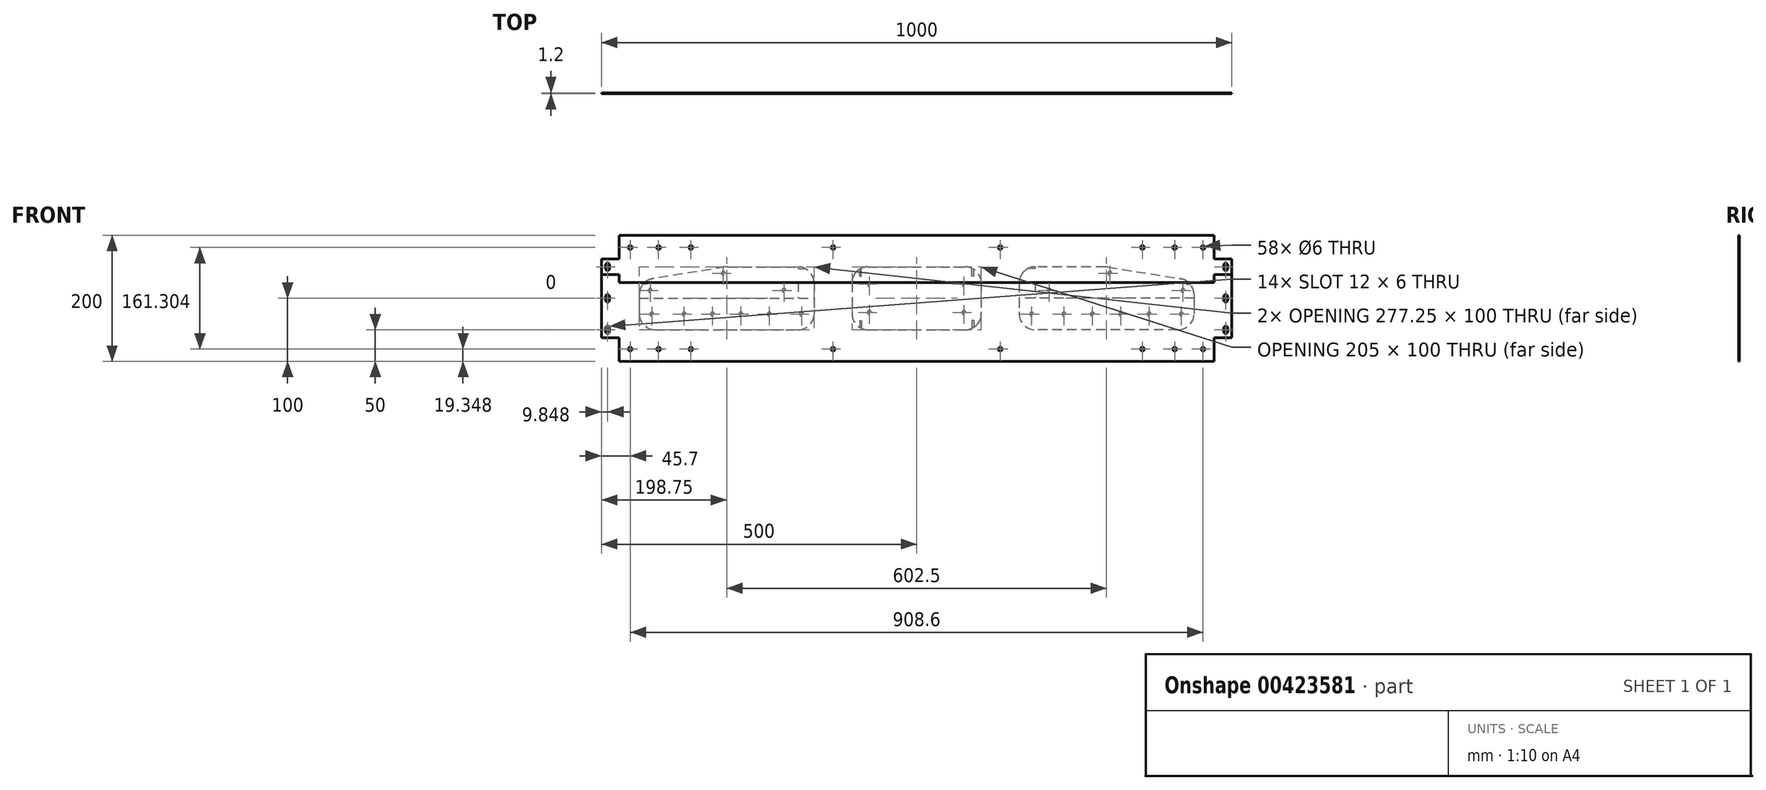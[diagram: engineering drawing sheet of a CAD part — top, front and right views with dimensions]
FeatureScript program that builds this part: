
annotation { "Feature Type Name" : "Feature", "Feature Type Description" : "" }
export const myFeature = defineFeature(function(context is Context, id is Id, definition is map)
    precondition{}
    {
        {
            assignVariable(context, id + "F0", {"name" : "eTole", "anyValue" : 0.8});
        }
        {
            var Q0;
            Q0=qCreatedBy(makeId("Front.planeOp"),FACE);
            var sketch = newSketch(context, id + "F1", { "sketchPlane" : qUnion([Q0])});
            skLineSegment(sketch, "E0.bottom", {"start": v(-471.9, 100) * mm, "end": v(471.9, 100) * mm});
            skLineSegment(sketch, "E0.top", {"start": v(-471.9, -100) * mm, "end": v(471.9, -100) * mm});
            skLineSegment(sketch, "E0.left", {"start": v(-500, 62.4) * mm, "end": v(-500, -62.4) * mm});
            skLineSegment(sketch, "E0.right", {"start": v(500, 62.4) * mm, "end": v(500, -62.4) * mm});
            skLineSegment(sketch, "E1.bottom", {"start": v(-471.9, 62.4) * mm, "end": v(471.9, 62.4) * mm, "construction": true});
            skLineSegment(sketch, "E1.top", {"start": v(-471.9, -62.4) * mm, "end": v(471.9, -62.4) * mm, "construction": true});
            skLineSegment(sketch, "E1.left", {"start": v(-471.9, 62.4) * mm, "end": v(-471.9, -62.4) * mm, "construction": true});
            skLineSegment(sketch, "E1.right", {"start": v(471.9, 62.4) * mm, "end": v(471.9, -62.4) * mm, "construction": true});
            skLineSegment(sketch, "E2.bottom", {"start": v(-77, 50) * mm, "end": v(77, 50) * mm});
            skLineSegment(sketch, "E2.top", {"start": v(-77, -50) * mm, "end": v(77, -50) * mm});
            skLineSegment(sketch, "E2.left", {"start": v(-102.5, 24.5) * mm, "end": v(-102.5, -24.5) * mm});
            skLineSegment(sketch, "E2.right", {"start": v(102.5, 24.5) * mm, "end": v(102.5, -24.5) * mm});
            skLineSegment(sketch, "E3", {"start": v(-102.5, 0) * mm, "end": v(-102.5, -100) * mm, "construction": true});
            skLineSegment(sketch, "E4.bottom", {"start": v(-75, 22.5) * mm, "end": v(75, 22.5) * mm, "construction": true});
            skLineSegment(sketch, "E4.top", {"start": v(-75, -22.5) * mm, "end": v(75, -22.5) * mm, "construction": true});
            skLineSegment(sketch, "E4.left", {"start": v(-75, 22.5) * mm, "end": v(-75, -22.5) * mm, "construction": true});
            skLineSegment(sketch, "E4.right", {"start": v(75, 22.5) * mm, "end": v(75, -22.5) * mm, "construction": true});
            skLineSegment(sketch, "E5", {"start": v(-102.5, 22.5) * mm, "end": v(-75, 22.5) * mm, "construction": true});
            skLineSegment(sketch, "E6", {"start": v(-75, 22.5) * mm, "end": v(-75, 50) * mm, "construction": true});
            skLineSegment(sketch, "E7.bottom", {"start": v(-299.22, 50) * mm, "end": v(-188.13, 50) * mm});
            skLineSegment(sketch, "E7.top", {"start": v(-414.38, -50) * mm, "end": v(-188.13, -50) * mm});
            skLineSegment(sketch, "E7.left", {"start": v(-439.87, 6.02) * mm, "end": v(-439.87, -24.5) * mm});
            skLineSegment(sketch, "E7.right", {"start": v(-162.63, 24.5) * mm, "end": v(-162.63, -24.5) * mm});
            skLineSegment(sketch, "E8", {"start": v(-162.63, -50) * mm, "end": v(-162.63, -62.4) * mm, "construction": true});
            skLineSegment(sketch, "E9", {"start": v(-162.63, -62.4) * mm, "end": v(-162.63, -87.6) * mm, "construction": true});
            skLineSegment(sketch, "E10", {"start": v(-162.63, -87.6) * mm, "end": v(-162.63, -100) * mm, "construction": true});
            skLineSegment(sketch, "E11", {"start": v(-500, 0) * mm, "end": v(-439.87, 0) * mm, "construction": true});
            skLineSegment(sketch, "E12", {"start": v(-162.63, 0) * mm, "end": v(-102.5, 0) * mm, "construction": true});
            skLineSegment(sketch, "E13", {"start": v(-500, -62.4) * mm, "end": v(-471.9, -62.4) * mm});
            skLineSegment(sketch, "E14", {"start": v(-471.9, -62.4) * mm, "end": v(-471.9, -100) * mm});
            skLineSegment(sketch, "E15", {"start": v(-303.26, 49.68) * mm, "end": v(-418.41, 31.2) * mm});
            skPoint(sketch, "E16.orphan", {"position": v(-439.87, 50) * mm});
            skPoint(sketch, "E17.visualSharp", {"position": v(-439.87, -50) * mm});
            skArc(sketch, "E17.filletArc", {"start": v(-439.88, -24.5) * mm, "mid": v(-432.4, -42.53) * mm, "end": v(-414.38, -50) * mm});
            skPoint(sketch, "E18.visualSharp", {"position": v(-439.88, 27.76) * mm});
            skArc(sketch, "E18.filletArc", {"start": v(-418.41, 31.2) * mm, "mid": v(-433.78, 22.56) * mm, "end": v(-439.88, 6.02) * mm});
            skPoint(sketch, "E19.visualSharp", {"position": v(-301.25, 50) * mm});
            skArc(sketch, "E19.filletArc", {"start": v(-299.22, 50) * mm, "mid": v(-301.24, 49.92) * mm, "end": v(-303.26, 49.68) * mm});
            skPoint(sketch, "E20.visualSharp", {"position": v(-162.63, 50) * mm});
            skArc(sketch, "E20.filletArc", {"start": v(-162.63, 24.5) * mm, "mid": v(-170.1, 42.53) * mm, "end": v(-188.13, 50) * mm});
            skPoint(sketch, "E21.visualSharp", {"position": v(-162.63, -50) * mm});
            skArc(sketch, "E21.filletArc", {"start": v(-188.13, -50) * mm, "mid": v(-170.1, -42.53) * mm, "end": v(-162.63, -24.5) * mm});
            skPoint(sketch, "E22.visualSharp", {"position": v(-102.5, -50) * mm});
            skArc(sketch, "E22.filletArc", {"start": v(-102.5, -24.5) * mm, "mid": v(-95.03, -42.53) * mm, "end": v(-77, -50) * mm});
            skPoint(sketch, "E23.visualSharp", {"position": v(102.5, -50) * mm});
            skArc(sketch, "E23.filletArc", {"start": v(77, -50) * mm, "mid": v(95.03, -42.53) * mm, "end": v(102.5, -24.5) * mm});
            skPoint(sketch, "E24.visualSharp", {"position": v(102.5, 50) * mm});
            skArc(sketch, "E24.filletArc", {"start": v(102.5, 24.5) * mm, "mid": v(95.03, 42.53) * mm, "end": v(77, 50) * mm});
            skPoint(sketch, "E25.visualSharp", {"position": v(-102.5, 50) * mm});
            skArc(sketch, "E25.filletArc", {"start": v(-77, 50) * mm, "mid": v(-95.03, 42.53) * mm, "end": v(-102.5, 24.5) * mm});
            skLineSegment(sketch, "E26", {"start": v(-418.41, 62.4) * mm, "end": v(-418.41, 0) * mm, "construction": true});
            skLineSegment(sketch, "E27.MirrorCS", {"start": v(-471.9, 62.4) * mm, "end": v(-471.9, 100) * mm});
            skLineSegment(sketch, "E28.MirrorCS", {"start": v(-500, 62.4) * mm, "end": v(-471.9, 62.4) * mm});
            skPoint(sketch, "E29.orphan", {"position": v(-500, 100) * mm});
            skPoint(sketch, "E30.orphan", {"position": v(-500, -100) * mm});
            skArc(sketch, "E31.MirrorCS", {"start": v(162.63, 24.5) * mm, "mid": v(170.1, 42.53) * mm, "end": v(188.13, 50) * mm});
            skLineSegment(sketch, "E32.MirrorCS", {"start": v(162.63, 24.5) * mm, "end": v(162.63, -24.5) * mm});
            skArc(sketch, "E33.MirrorCS", {"start": v(188.13, -50) * mm, "mid": v(170.1, -42.53) * mm, "end": v(162.63, -24.5) * mm});
            skLineSegment(sketch, "E34.MirrorCS", {"start": v(414.38, -50) * mm, "end": v(188.13, -50) * mm});
            skArc(sketch, "E35.MirrorCS", {"start": v(439.88, -24.5) * mm, "mid": v(432.4, -42.53) * mm, "end": v(414.38, -50) * mm});
            skLineSegment(sketch, "E36.MirrorCS", {"start": v(439.87, 6.02) * mm, "end": v(439.87, -24.5) * mm});
            skArc(sketch, "E37.MirrorCS", {"start": v(418.41, 31.2) * mm, "mid": v(433.78, 22.56) * mm, "end": v(439.88, 6.02) * mm});
            skLineSegment(sketch, "E38.MirrorCS", {"start": v(303.26, 49.68) * mm, "end": v(418.41, 31.2) * mm});
            skLineSegment(sketch, "E39.MirrorCS", {"start": v(299.22, 50) * mm, "end": v(188.13, 50) * mm});
            skArc(sketch, "E40.MirrorCS", {"start": v(299.22, 50) * mm, "mid": v(301.24, 49.92) * mm, "end": v(303.26, 49.68) * mm});
            skLineSegment(sketch, "E41.MirrorCS", {"start": v(500, -62.4) * mm, "end": v(471.9, -62.4) * mm});
            skLineSegment(sketch, "E42.MirrorCS", {"start": v(471.9, -62.4) * mm, "end": v(471.9, -100) * mm});
            skLineSegment(sketch, "E43.MirrorCS", {"start": v(500, 62.4) * mm, "end": v(471.9, 62.4) * mm});
            skLineSegment(sketch, "E44.MirrorCS", {"start": v(471.9, 62.4) * mm, "end": v(471.9, 100) * mm});
            skSolve(sketch);
        }
        {
            var Q0;
            Q0=qCreatedBy(makeId("Front.planeOp"),FACE);
            var sketch = newSketch(context, id + "F2", { "sketchPlane" : qUnion([Q0])});
            skLineSegment(sketch, "E45.0", {"start": v(-414.38, -50) * mm, "end": v(-188.13, -50) * mm});
            skArc(sketch, "E45.1", {"start": v(-439.88, -24.5) * mm, "mid": v(-432.4, -42.53) * mm, "end": v(-414.38, -50) * mm});
            skLineSegment(sketch, "E45.2", {"start": v(-439.87, 0) * mm, "end": v(-439.87, -24.5) * mm});
            skArc(sketch, "E45.3", {"start": v(-188.13, -50) * mm, "mid": v(-170.1, -42.53) * mm, "end": v(-162.63, -24.5) * mm});
            skLineSegment(sketch, "E45.4", {"start": v(-162.63, 0) * mm, "end": v(-162.63, -24.5) * mm});
            skLineSegment(sketch, "E45.5", {"start": v(-439.87, 0) * mm, "end": v(-162.63, 0) * mm});
            skLineSegment(sketch, "E46.0", {"start": v(-162.63, -62.4) * mm, "end": v(-162.63, -87.6) * mm, "construction": true});
            skLineSegment(sketch, "E47.MirrorCS", {"start": v(-162.63, -37.6) * mm, "end": v(-162.63, -12.4) * mm, "construction": true});
            skLineSegment(sketch, "E48", {"start": v(-162.63, -37.6) * mm, "end": v(-439.87, -37.6) * mm, "construction": true});
            skLineSegment(sketch, "E49", {"start": v(-439.87, -12.4) * mm, "end": v(-162.63, -12.4) * mm, "construction": true});
            skLineSegment(sketch, "E50", {"start": v(-301.25, 0) * mm, "end": v(-301.25, -50) * mm, "construction": true});
            skLineSegment(sketch, "E51.0", {"start": v(-75, 22.5) * mm, "end": v(-75, -22.5) * mm, "construction": true});
            skLineSegment(sketch, "E52", {"start": v(-323.75, -25) * mm, "end": v(-278.75, -25) * mm, "construction": true});
            skCircle(sketch, "E53", {"center": v(-323.75, -25) * mm, "radius": 3 * mm});
            skCircle(sketch, "E54", {"center": v(-278.75, -25) * mm, "radius": 3 * mm});
            skCircle(sketch, "E55", {"center": v(-419.98, -25) * mm, "radius": 3 * mm});
            skCircle(sketch, "E56", {"center": v(-182.53, -25) * mm, "radius": 3 * mm});
            skLineSegment(sketch, "E57", {"start": v(-278.75, -25) * mm, "end": v(-233.75, -25) * mm, "construction": true});
            skCircle(sketch, "E58", {"center": v(-233.75, -25) * mm, "radius": 3 * mm});
            skCircle(sketch, "E59.MirrorC", {"center": v(-368.75, -25) * mm, "radius": 3 * mm});
            skSolve(sketch);
        }
        {
            var Q0;
            Q0=qCreatedBy(makeId("Front.planeOp"),FACE);
            var sketch = newSketch(context, id + "F3", { "sketchPlane" : qUnion([Q0])});
            skArc(sketch, "E60.0", {"start": v(-77, 50) * mm, "mid": v(-82.37, 49.43) * mm, "end": v(-87.5, 47.74) * mm});
            skLineSegment(sketch, "E60.1", {"start": v(-77, 50) * mm, "end": v(77, 50) * mm});
            skArc(sketch, "E60.2", {"start": v(102.5, 24.5) * mm, "mid": v(99.3, 36.87) * mm, "end": v(90.5, 46.13) * mm});
            skLineSegment(sketch, "E60.3", {"start": v(102.5, 24.5) * mm, "end": v(102.5, -24.5) * mm});
            skArc(sketch, "E60.4", {"start": v(77, -50) * mm, "mid": v(82.37, -49.43) * mm, "end": v(87.5, -47.74) * mm});
            skLineSegment(sketch, "E60.5", {"start": v(-77, -50) * mm, "end": v(77, -50) * mm});
            skArc(sketch, "E60.6", {"start": v(-102.5, -24.5) * mm, "mid": v(-99.3, -36.87) * mm, "end": v(-90.5, -46.13) * mm});
            skLineSegment(sketch, "E60.7", {"start": v(-102.5, 24.5) * mm, "end": v(-102.5, -24.5) * mm});
            skPoint(sketch, "E61.0", {"position": v(-75, 22.5) * mm});
            skPoint(sketch, "E61.1", {"position": v(75, 22.5) * mm});
            skPoint(sketch, "E61.2", {"position": v(75, -22.5) * mm});
            skPoint(sketch, "E61.3", {"position": v(-75, -22.5) * mm});
            skCircle(sketch, "E62", {"center": v(-75, 22.5) * mm, "radius": 3 * mm});
            skCircle(sketch, "E63", {"center": v(-75, -22.5) * mm, "radius": 3 * mm});
            skCircle(sketch, "E64", {"center": v(75, 22.5) * mm, "radius": 3 * mm});
            skCircle(sketch, "E65", {"center": v(75, -22.5) * mm, "radius": 3 * mm});
            skLineSegment(sketch, "E66.bottom", {"start": v(-87.5, 35) * mm, "end": v(87.5, 35) * mm, "construction": true});
            skLineSegment(sketch, "E66.top", {"start": v(-87.5, -35) * mm, "end": v(87.5, -35) * mm, "construction": true});
            skLineSegment(sketch, "E66.left", {"start": v(-87.5, 35) * mm, "end": v(-87.5, -35) * mm, "construction": true});
            skLineSegment(sketch, "E66.right", {"start": v(87.5, 35) * mm, "end": v(87.5, -35) * mm, "construction": true});
            skLineSegment(sketch, "E67", {"start": v(0, 35) * mm, "end": v(0, 50) * mm, "construction": true});
            skLineSegment(sketch, "E68", {"start": v(-102.5, 0) * mm, "end": v(-87.5, 0) * mm, "construction": true});
            skLineSegment(sketch, "E69.bottom", {"start": v(-90.5, 35) * mm, "end": v(-87.5, 35) * mm});
            skLineSegment(sketch, "E69.left", {"start": v(-87.5, 35) * mm, "end": v(-87.5, 47.74) * mm});
            skLineSegment(sketch, "E69.right", {"start": v(-90.5, 35) * mm, "end": v(-90.5, 46.13) * mm});
            skArc(sketch, "E70.trimOffspring", {"start": v(-90.5, 46.13) * mm, "mid": v(-99.3, 36.87) * mm, "end": v(-102.5, 24.5) * mm});
            skLineSegment(sketch, "E71.MirrorCS", {"start": v(90.5, 35) * mm, "end": v(90.5, 46.13) * mm});
            skLineSegment(sketch, "E72.MirrorCS", {"start": v(87.5, 35) * mm, "end": v(87.5, 47.74) * mm});
            skLineSegment(sketch, "E73.MirrorCS", {"start": v(90.5, 35) * mm, "end": v(87.5, 35) * mm});
            skArc(sketch, "E74.trimOffspring", {"start": v(87.5, 47.74) * mm, "mid": v(82.37, 49.43) * mm, "end": v(77, 50) * mm});
            skLineSegment(sketch, "E75.MirrorCS", {"start": v(90.5, -35) * mm, "end": v(90.5, -46.13) * mm});
            skLineSegment(sketch, "E76.MirrorCS", {"start": v(87.5, -35) * mm, "end": v(87.5, -47.74) * mm});
            skLineSegment(sketch, "E77.MirrorCS", {"start": v(90.5, -35) * mm, "end": v(87.5, -35) * mm});
            skLineSegment(sketch, "E78.MirrorCS", {"start": v(-87.5, -35) * mm, "end": v(-87.5, -47.74) * mm});
            skLineSegment(sketch, "E79.MirrorCS", {"start": v(-90.5, -35) * mm, "end": v(-90.5, -46.13) * mm});
            skLineSegment(sketch, "E80.MirrorCS", {"start": v(-90.5, -35) * mm, "end": v(-87.5, -35) * mm});
            skArc(sketch, "E81.trimOffspring", {"start": v(-87.5, -47.74) * mm, "mid": v(-82.37, -49.43) * mm, "end": v(-77, -50) * mm});
            skArc(sketch, "E82.trimOffspring", {"start": v(90.5, -46.13) * mm, "mid": v(99.3, -36.87) * mm, "end": v(102.5, -24.5) * mm});
            skSolve(sketch);
        }
        {
            var Q0;
            Q0=qCreatedBy(makeId("Front.planeOp"),FACE);
            var sketch = newSketch(context, id + "F4", { "sketchPlane" : qUnion([Q0])});
            skArc(sketch, "E83.1", {"start": v(-162.63, 25.2) * mm, "mid": v(-166.44, 37.92) * mm, "end": v(-176.12, 47) * mm});
            skArc(sketch, "E83.2", {"start": v(-299.22, 50) * mm, "mid": v(-301.24, 49.92) * mm, "end": v(-303.26, 49.68) * mm});
            skLineSegment(sketch, "E83.3", {"start": v(-303.26, 49.68) * mm, "end": v(-418.41, 31.2) * mm});
            skLineSegment(sketch, "E83.4", {"start": v(-439.87, 0) * mm, "end": v(-187.83, 0) * mm});
            skLineSegment(sketch, "E83.5", {"start": v(-439.87, 6.02) * mm, "end": v(-439.87, 0) * mm});
            skArc(sketch, "E83.6", {"start": v(-418.41, 31.2) * mm, "mid": v(-425.22, 29.1) * mm, "end": v(-431.18, 25.2) * mm});
            skLineSegment(sketch, "E83.7", {"start": v(-299.22, 50) * mm, "end": v(-187.83, 50) * mm});
            skLineSegment(sketch, "E84", {"start": v(-187.83, 50) * mm, "end": v(-187.83, 25.2) * mm, "construction": true});
            skLineSegment(sketch, "E85", {"start": v(-187.83, 25.2) * mm, "end": v(-187.83, 0) * mm});
            skLineSegment(sketch, "E86", {"start": v(-187.83, 25.2) * mm, "end": v(-162.63, 25.2) * mm});
            skLineSegment(sketch, "E87", {"start": v(-187.83, 25.2) * mm, "end": v(-431.18, 25.2) * mm, "construction": true});
            skLineSegment(sketch, "E88.0", {"start": v(-75, 22.5) * mm, "end": v(-75, -22.5) * mm, "construction": true});
            skLineSegment(sketch, "E89.0", {"start": v(-278.75, -25) * mm, "end": v(-233.75, -25) * mm, "construction": true});
            skPoint(sketch, "E89.1", {"position": v(-182.53, -25) * mm});
            skCircle(sketch, "E89.2", {"center": v(-278.75, -25) * mm, "radius": 3 * mm, "construction": true});
            skPoint(sketch, "E89.3", {"position": v(-301.25, -25) * mm});
            skLineSegment(sketch, "E90.0", {"start": v(-162.63, -37.6) * mm, "end": v(-162.63, -12.4) * mm, "construction": true});
            skLineSegment(sketch, "E91", {"start": v(-301.25, -25) * mm, "end": v(-278.75, -25) * mm, "construction": true});
            skLineSegment(sketch, "E92", {"start": v(-187.83, 12.6) * mm, "end": v(-210.33, 12.6) * mm, "construction": true});
            skCircle(sketch, "E93", {"center": v(-210.33, 12.6) * mm, "radius": 3 * mm});
            skCircle(sketch, "E94", {"center": v(-422.48, 12.6) * mm, "radius": 3 * mm});
            skLineSegment(sketch, "E95", {"start": v(-187.83, 50) * mm, "end": v(-187.83, 47) * mm});
            skLineSegment(sketch, "E96", {"start": v(-187.83, 47) * mm, "end": v(-176.12, 47) * mm});
            skPoint(sketch, "E97.orphan", {"position": v(-188.13, 50) * mm});
            skPoint(sketch, "E98.oppositeSnap0", {"position": v(-434.09, 22.2) * mm});
            skLineSegment(sketch, "E98.bottom", {"start": v(-428.18, 25.2) * mm, "end": v(-431.18, 25.2) * mm});
            skLineSegment(sketch, "E98.top", {"start": v(-428.18, 22.2) * mm, "end": v(-434.09, 22.2) * mm});
            skLineSegment(sketch, "E98.left", {"start": v(-428.18, 25.2) * mm, "end": v(-428.18, 22.2) * mm});
            skArc(sketch, "E99.trimOffspring", {"start": v(-434.09, 22.2) * mm, "mid": v(-438.38, 14.61) * mm, "end": v(-439.88, 6.02) * mm});
            skLineSegment(sketch, "E100", {"start": v(-233.75, -25) * mm, "end": v(-182.53, -25) * mm, "construction": true});
            skLineSegment(sketch, "E101", {"start": v(-210.33, 12.6) * mm, "end": v(-255.33, 12.6) * mm, "construction": true});
            skLineSegment(sketch, "E102", {"start": v(-255.33, 12.6) * mm, "end": v(-306.56, 12.6) * mm, "construction": true});
            skCircle(sketch, "E103", {"center": v(-306.56, 39.83) * mm, "radius": 3 * mm});
            skPoint(sketch, "E104.orphan", {"position": v(-162.63, 24.5) * mm});
            skSolve(sketch);
        }
        {
            var Q0;
            Q0=qCreatedBy(makeId("Front.planeOp"),FACE);
            var sketch = newSketch(context, id + "F5", { "sketchPlane" : qUnion([Q0])});
            skLineSegment(sketch, "E105.0", {"start": v(-471.9, 62.4) * mm, "end": v(471.9, 62.4) * mm, "construction": true});
            skLineSegment(sketch, "E105.1", {"start": v(-471.9, 62.4) * mm, "end": v(-471.9, -62.4) * mm, "construction": true});
            skLineSegment(sketch, "E106.0", {"start": v(-278.75, -25) * mm, "end": v(-233.75, -25) * mm, "construction": true});
            skPoint(sketch, "E106.1", {"position": v(-182.53, -25) * mm});
            skLineSegment(sketch, "E106.2", {"start": v(-323.75, -25) * mm, "end": v(-278.75, -25) * mm, "construction": true});
            skCircle(sketch, "E106.3", {"center": v(-278.75, -25) * mm, "radius": 3 * mm, "construction": true});
            skLineSegment(sketch, "E107", {"start": v(-471.9, 62.4) * mm, "end": v(-471.9, 80.65) * mm, "construction": true});
            skLineSegment(sketch, "E108", {"start": v(-499.3, 80.65) * mm, "end": v(-454.3, 80.65) * mm, "construction": true});
            skLineSegment(sketch, "E109", {"start": v(-454.3, 80.65) * mm, "end": v(-409.3, 80.65) * mm, "construction": true});
            skLineSegment(sketch, "E110", {"start": v(-409.3, 80.65) * mm, "end": v(-358.07, 80.65) * mm, "construction": true});
            skCircle(sketch, "E111", {"center": v(-454.3, 80.65) * mm, "radius": 3 * mm});
            skCircle(sketch, "E112", {"center": v(-409.3, 80.65) * mm, "radius": 3 * mm});
            skCircle(sketch, "E113", {"center": v(-358.07, 80.65) * mm, "radius": 3 * mm});
            skLineSegment(sketch, "E114", {"start": v(-233.75, -25) * mm, "end": v(-182.53, -25) * mm, "construction": true});
            skPoint(sketch, "E115.0", {"position": v(-132.56, 0) * mm});
            skCircle(sketch, "E116", {"center": v(-132.56, 80.65) * mm, "radius": 3 * mm});
            skLineSegment(sketch, "E117.0", {"start": v(-162.63, -37.6) * mm, "end": v(-162.63, -12.4) * mm, "construction": true});
            skLineSegment(sketch, "E118", {"start": v(-409.3, 62.4) * mm, "end": v(-409.3, 68.05) * mm, "construction": true});
            skLineSegment(sketch, "E119", {"start": v(-409.3, 68.05) * mm, "end": v(-409.3, 93.25) * mm, "construction": true});
            skLineSegment(sketch, "E120", {"start": v(-471.9, 62.4) * mm, "end": v(-490.15, 62.4) * mm, "construction": true});
            skLineSegment(sketch, "E121", {"start": v(-490.15, 62.4) * mm, "end": v(-490.15, -62.4) * mm, "construction": true});
            skArc(sketch, "E122", {"start": v(-487.15, 53) * mm, "mid": v(-490.15, 56) * mm, "end": v(-493.15, 53) * mm});
            skLineSegment(sketch, "E123", {"start": v(-493.15, 53) * mm, "end": v(-493.15, 47) * mm});
            skLineSegment(sketch, "E124", {"start": v(-487.15, 47) * mm, "end": v(-487.15, 53) * mm});
            skArc(sketch, "E125", {"start": v(-493.15, 47) * mm, "mid": v(-490.15, 44) * mm, "end": v(-487.15, 47) * mm});
            skLineSegment(sketch, "E126", {"start": v(-487.15, 50) * mm, "end": v(-487.15, 62.4) * mm, "construction": true});
            skLineSegment(sketch, "E127.0.1.0", {"start": v(-487.15, -3) * mm, "end": v(-487.15, 3) * mm});
            skArc(sketch, "E127.0.1.1", {"start": v(-493.15, -3) * mm, "mid": v(-490.15, -6) * mm, "end": v(-487.15, -3) * mm});
            skLineSegment(sketch, "E127.0.1.2", {"start": v(-493.15, 3) * mm, "end": v(-493.15, -3) * mm});
            skArc(sketch, "E127.0.1.3", {"start": v(-487.15, 3) * mm, "mid": v(-490.15, 6) * mm, "end": v(-493.15, 3) * mm});
            skLineSegment(sketch, "E127.0.1.4", {"start": v(-487.15, 0) * mm, "end": v(-487.15, 12.4) * mm, "construction": true});
            skLineSegment(sketch, "E127.0.1.5", {"start": v(-471.9, 12.4) * mm, "end": v(-490.15, 12.4) * mm, "construction": true});
            skLineSegment(sketch, "E127.0.2.0", {"start": v(-487.15, -53) * mm, "end": v(-487.15, -47) * mm});
            skArc(sketch, "E127.0.2.1", {"start": v(-493.15, -53) * mm, "mid": v(-490.15, -56) * mm, "end": v(-487.15, -53) * mm});
            skLineSegment(sketch, "E127.0.2.2", {"start": v(-493.15, -47) * mm, "end": v(-493.15, -53) * mm});
            skArc(sketch, "E127.0.2.3", {"start": v(-487.15, -47) * mm, "mid": v(-490.15, -44) * mm, "end": v(-493.15, -47) * mm});
            skLineSegment(sketch, "E127.0.2.4", {"start": v(-487.15, -50) * mm, "end": v(-487.15, -37.6) * mm, "construction": true});
            skLineSegment(sketch, "E127.0.2.5", {"start": v(-471.9, -37.6) * mm, "end": v(-490.15, -37.6) * mm, "construction": true});
            skLineSegment(sketch, "E127.direction1", {"start": v(-487.15, 47) * mm, "end": v(-465.92, 47) * mm, "construction": true});
            skLineSegment(sketch, "E127.direction2", {"start": v(-487.15, 47) * mm, "end": v(-487.15, -3) * mm, "construction": true});
            skLineSegment(sketch, "E128", {"start": v(-487.15, -50) * mm, "end": v(-487.15, -62.4) * mm, "construction": true});
            skCircle(sketch, "E129.MirrorC", {"center": v(132.56, 80.65) * mm, "radius": 3 * mm});
            skCircle(sketch, "E130.MirrorC", {"center": v(358.07, 80.65) * mm, "radius": 3 * mm});
            skCircle(sketch, "E131.MirrorC", {"center": v(409.3, 80.65) * mm, "radius": 3 * mm});
            skCircle(sketch, "E132.MirrorC", {"center": v(454.3, 80.65) * mm, "radius": 3 * mm});
            skArc(sketch, "E133.MirrorCS", {"start": v(493.15, -53) * mm, "mid": v(490.15, -56) * mm, "end": v(487.15, -53) * mm});
            skLineSegment(sketch, "E134.MirrorCS", {"start": v(493.15, -47) * mm, "end": v(493.15, -53) * mm});
            skArc(sketch, "E135.MirrorCS", {"start": v(487.15, -47) * mm, "mid": v(490.15, -44) * mm, "end": v(493.15, -47) * mm});
            skArc(sketch, "E136.MirrorCS", {"start": v(493.15, -3) * mm, "mid": v(490.15, -6) * mm, "end": v(487.15, -3) * mm});
            skLineSegment(sketch, "E137.MirrorCS", {"start": v(493.15, 3) * mm, "end": v(493.15, -3) * mm});
            skArc(sketch, "E138.MirrorCS", {"start": v(487.15, 3) * mm, "mid": v(490.15, 6) * mm, "end": v(493.15, 3) * mm});
            skArc(sketch, "E139.MirrorCS", {"start": v(493.15, 47) * mm, "mid": v(490.15, 44) * mm, "end": v(487.15, 47) * mm});
            skLineSegment(sketch, "E140.MirrorCS", {"start": v(493.15, 53) * mm, "end": v(493.15, 47) * mm});
            skArc(sketch, "E141.MirrorCS", {"start": v(487.15, 53) * mm, "mid": v(490.15, 56) * mm, "end": v(493.15, 53) * mm});
            skLineSegment(sketch, "E142.MirrorCS", {"start": v(487.15, 47) * mm, "end": v(487.15, 53) * mm});
            skLineSegment(sketch, "E143.MirrorCS", {"start": v(487.15, -3) * mm, "end": v(487.15, 3) * mm});
            skLineSegment(sketch, "E144.MirrorCS", {"start": v(487.15, -53) * mm, "end": v(487.15, -47) * mm});
            skCircle(sketch, "E145.MirrorC", {"center": v(-358.07, -80.65) * mm, "radius": 3 * mm});
            skCircle(sketch, "E146.MirrorC", {"center": v(132.56, -80.65) * mm, "radius": 3 * mm});
            skCircle(sketch, "E147.MirrorC", {"center": v(358.07, -80.65) * mm, "radius": 3 * mm});
            skCircle(sketch, "E148.MirrorC", {"center": v(409.3, -80.65) * mm, "radius": 3 * mm});
            skCircle(sketch, "E149.MirrorC", {"center": v(454.3, -80.65) * mm, "radius": 3 * mm});
            skCircle(sketch, "E150.MirrorC", {"center": v(-132.56, -80.65) * mm, "radius": 3 * mm});
            skCircle(sketch, "E151.MirrorC", {"center": v(-454.3, -80.65) * mm, "radius": 3 * mm});
            skCircle(sketch, "E152.MirrorC", {"center": v(-409.3, -80.65) * mm, "radius": 3 * mm});
            skLineSegment(sketch, "E153", {"start": v(-471.9, 80.65) * mm, "end": v(-476.8, 80.65) * mm, "construction": true});
            skSolve(sketch);
        }
        {
            var Q0;
            Q0=qCreatedBy(makeId("Front.planeOp"),FACE);
            var sketch = newSketch(context, id + "F6", { "sketchPlane" : qUnion([Q0])});
            skCircle(sketch, "E154.13", {"center": v(409.3, 80.65) * mm, "radius": 3 * mm});
            skCircle(sketch, "E154.14", {"center": v(-409.3, -80.65) * mm, "radius": 3 * mm});
            skCircle(sketch, "E154.15", {"center": v(358.07, -80.65) * mm, "radius": 3 * mm});
            skCircle(sketch, "E154.16", {"center": v(-132.56, -80.65) * mm, "radius": 3 * mm});
            skCircle(sketch, "E154.17", {"center": v(454.3, -80.65) * mm, "radius": 3 * mm});
            skCircle(sketch, "E154.18", {"center": v(-358.07, -80.65) * mm, "radius": 3 * mm});
            skCircle(sketch, "E154.19", {"center": v(358.07, 80.65) * mm, "radius": 3 * mm});
            skCircle(sketch, "E154.21", {"center": v(409.3, -80.65) * mm, "radius": 3 * mm});
            skCircle(sketch, "E154.22", {"center": v(-132.56, 80.65) * mm, "radius": 3 * mm});
            skCircle(sketch, "E154.23", {"center": v(-454.3, -80.65) * mm, "radius": 3 * mm});
            skCircle(sketch, "E154.24", {"center": v(132.56, 80.65) * mm, "radius": 3 * mm});
            skCircle(sketch, "E154.25", {"center": v(454.3, 80.65) * mm, "radius": 3 * mm});
            skCircle(sketch, "E154.26", {"center": v(132.56, -80.65) * mm, "radius": 3 * mm});
            skCircle(sketch, "E154.27", {"center": v(-454.3, 80.65) * mm, "radius": 3 * mm});
            skCircle(sketch, "E154.28", {"center": v(-409.3, 80.65) * mm, "radius": 3 * mm});
            skCircle(sketch, "E154.29", {"center": v(-358.07, 80.65) * mm, "radius": 3 * mm});
            skLineSegment(sketch, "E155.0", {"start": v(-471.9, 100) * mm, "end": v(471.9, 100) * mm});
            skLineSegment(sketch, "E155.1", {"start": v(-500, 62.4) * mm, "end": v(-500, -62.4) * mm});
            skLineSegment(sketch, "E155.2", {"start": v(-471.9, 62.4) * mm, "end": v(-471.9, 100) * mm});
            skLineSegment(sketch, "E155.3", {"start": v(-500, 62.4) * mm, "end": v(-471.9, 62.4) * mm});
            skLineSegment(sketch, "E155.4", {"start": v(-500, -62.4) * mm, "end": v(-471.9, -62.4) * mm});
            skLineSegment(sketch, "E155.5", {"start": v(-471.9, -62.4) * mm, "end": v(-471.9, -100) * mm});
            skLineSegment(sketch, "E155.6", {"start": v(-471.9, -100) * mm, "end": v(471.9, -100) * mm});
            skLineSegment(sketch, "E155.7", {"start": v(471.9, -62.4) * mm, "end": v(471.9, -100) * mm});
            skLineSegment(sketch, "E155.8", {"start": v(500, -62.4) * mm, "end": v(471.9, -62.4) * mm});
            skLineSegment(sketch, "E155.9", {"start": v(500, 62.4) * mm, "end": v(500, -62.4) * mm});
            skLineSegment(sketch, "E155.10", {"start": v(500, 62.4) * mm, "end": v(471.9, 62.4) * mm});
            skLineSegment(sketch, "E155.11", {"start": v(471.9, 62.4) * mm, "end": v(471.9, 100) * mm});
            skArc(sketch, "E156.0", {"start": v(-487.15, 53) * mm, "mid": v(-490.15, 56) * mm, "end": v(-493.15, 53) * mm});
            skArc(sketch, "E156.1", {"start": v(-493.15, 47) * mm, "mid": v(-490.15, 44) * mm, "end": v(-487.15, 47) * mm});
            skLineSegment(sketch, "E156.2", {"start": v(-493.15, 53) * mm, "end": v(-493.15, 47) * mm});
            skArc(sketch, "E156.3", {"start": v(-487.15, 3) * mm, "mid": v(-490.15, 6) * mm, "end": v(-493.15, 3) * mm});
            skLineSegment(sketch, "E156.4", {"start": v(-493.15, 3) * mm, "end": v(-493.15, -3) * mm});
            skPoint(sketch, "E156.5", {"position": v(-487.15, 3) * mm});
            skArc(sketch, "E156.6", {"start": v(-493.15, -3) * mm, "mid": v(-490.15, -6) * mm, "end": v(-487.15, -3) * mm});
            skArc(sketch, "E156.7", {"start": v(-487.15, -47) * mm, "mid": v(-490.15, -44) * mm, "end": v(-493.15, -47) * mm});
            skArc(sketch, "E156.8", {"start": v(-493.15, -53) * mm, "mid": v(-490.15, -56) * mm, "end": v(-487.15, -53) * mm});
            skLineSegment(sketch, "E156.9", {"start": v(-493.15, -47) * mm, "end": v(-493.15, -53) * mm});
            skLineSegment(sketch, "E156.10", {"start": v(-487.15, -53) * mm, "end": v(-487.15, -47) * mm});
            skPoint(sketch, "E156.11", {"position": v(-487.15, 50) * mm});
            skLineSegment(sketch, "E157.0", {"start": v(487.15, 47) * mm, "end": v(487.15, 53) * mm});
            skLineSegment(sketch, "E157.1", {"start": v(493.15, 3) * mm, "end": v(493.15, -3) * mm});
            skLineSegment(sketch, "E157.2", {"start": v(493.15, -47) * mm, "end": v(493.15, -53) * mm});
            skArc(sketch, "E157.3", {"start": v(493.15, 47) * mm, "mid": v(490.15, 44) * mm, "end": v(487.15, 47) * mm});
            skArc(sketch, "E157.4", {"start": v(487.15, 53) * mm, "mid": v(490.15, 56) * mm, "end": v(493.15, 53) * mm});
            skLineSegment(sketch, "E157.5", {"start": v(493.15, 53) * mm, "end": v(493.15, 47) * mm});
            skLineSegment(sketch, "E157.6", {"start": v(487.15, -3) * mm, "end": v(487.15, 3) * mm});
            skArc(sketch, "E157.7", {"start": v(487.15, -47) * mm, "mid": v(490.15, -44) * mm, "end": v(493.15, -47) * mm});
            skLineSegment(sketch, "E157.8", {"start": v(487.15, -53) * mm, "end": v(487.15, -47) * mm});
            skArc(sketch, "E157.9", {"start": v(487.15, 3) * mm, "mid": v(490.15, 6) * mm, "end": v(493.15, 3) * mm});
            skArc(sketch, "E157.10", {"start": v(493.15, -3) * mm, "mid": v(490.15, -6) * mm, "end": v(487.15, -3) * mm});
            skArc(sketch, "E157.11", {"start": v(493.15, -53) * mm, "mid": v(490.15, -56) * mm, "end": v(487.15, -53) * mm});
            skLineSegment(sketch, "E158.0", {"start": v(-487.15, -3) * mm, "end": v(-487.15, 3) * mm});
            skLineSegment(sketch, "E159.0", {"start": v(-487.15, 47) * mm, "end": v(-487.15, 53) * mm});
            skSolve(sketch);
        }
        {
            var Q0;
            Q0=qCreatedBy(makeId("Front.planeOp"),FACE);
            var sketch = newSketch(context, id + "F7", { "sketchPlane" : qUnion([Q0])});
            skLineSegment(sketch, "E160.0.0", {"start": v(500, 37.6) * mm, "end": v(500, 62.4) * mm});
            skLineSegment(sketch, "E160.0.1", {"start": v(500, 62.4) * mm, "end": v(471.9, 62.4) * mm});
            skLineSegment(sketch, "E160.0.2", {"start": v(471.9, 62.4) * mm, "end": v(471.9, 100) * mm});
            skLineSegment(sketch, "E160.0.3", {"start": v(471.9, 100) * mm, "end": v(-471.9, 100) * mm});
            skLineSegment(sketch, "E160.0.4", {"start": v(-471.9, 100) * mm, "end": v(-471.9, 62.4) * mm});
            skLineSegment(sketch, "E160.0.5", {"start": v(-471.9, 62.4) * mm, "end": v(-500, 62.4) * mm});
            skLineSegment(sketch, "E160.0.6", {"start": v(-500, 62.4) * mm, "end": v(-500, 37.6) * mm});
            skLineSegment(sketch, "E161", {"start": v(-471.9, 25) * mm, "end": v(471.9, 25) * mm});
            skLineSegment(sketch, "E162", {"start": v(-500, 37.6) * mm, "end": v(-471.9, 37.6) * mm});
            skLineSegment(sketch, "E163", {"start": v(-471.9, 37.6) * mm, "end": v(-471.9, 25) * mm});
            skLineSegment(sketch, "E164.MirrorCS", {"start": v(500, 37.6) * mm, "end": v(471.9, 37.6) * mm});
            skLineSegment(sketch, "E165.MirrorCS", {"start": v(471.9, 37.6) * mm, "end": v(471.9, 25) * mm});
            skArc(sketch, "E166.0", {"start": v(-487.15, 53) * mm, "mid": v(-490.15, 56) * mm, "end": v(-493.15, 53) * mm});
            skArc(sketch, "E167.0", {"start": v(-493.15, 47) * mm, "mid": v(-490.15, 44) * mm, "end": v(-487.15, 47) * mm});
            skCircle(sketch, "E168.0", {"center": v(-454.3, 80.65) * mm, "radius": 3 * mm});
            skCircle(sketch, "E169.0", {"center": v(-132.56, 80.65) * mm, "radius": 3 * mm});
            skCircle(sketch, "E170.0", {"center": v(454.3, 80.65) * mm, "radius": 3 * mm});
            skPoint(sketch, "E171.0", {"position": v(487.15, 50) * mm});
            skPoint(sketch, "E172.0", {"position": v(493.15, 50) * mm});
            skLineSegment(sketch, "E173.0", {"start": v(487.15, 47) * mm, "end": v(487.15, 53) * mm});
            skLineSegment(sketch, "E174.0", {"start": v(493.15, 53) * mm, "end": v(493.15, 47) * mm});
            skArc(sketch, "E175.0", {"start": v(487.15, 53) * mm, "mid": v(490.15, 56) * mm, "end": v(493.15, 53) * mm});
            skArc(sketch, "E176.0", {"start": v(493.15, 47) * mm, "mid": v(490.15, 44) * mm, "end": v(487.15, 47) * mm});
            skCircle(sketch, "E177.0", {"center": v(132.56, 80.65) * mm, "radius": 3 * mm});
            skLineSegment(sketch, "E178.0", {"start": v(-493.15, 53) * mm, "end": v(-493.15, 47) * mm});
            skLineSegment(sketch, "E179.0", {"start": v(-487.15, 47) * mm, "end": v(-487.15, 53) * mm});
            skLineSegment(sketch, "E180", {"start": v(-490.15, 53) * mm, "end": v(-490.15, 62.4) * mm, "construction": true});
            skLineSegment(sketch, "E181", {"start": v(-490.15, 47) * mm, "end": v(-490.15, 37.6) * mm, "construction": true});
            skSolve(sketch);
        }
        {
            var Q0;
            Q0 = qSketchRegion(id + "F1", true);
            var Q1;
            Q1 = qSketchRegion(id + "F2", true);
            var Q2;
            Q2 = qSketchRegion(id + "F3", true);
            var Q3;
            Q3 = qSketchRegion(id + "F4", true);
            extrude(context, id + "F8", {"entities" : qUnion([Q0, Q1, Q2, Q3]), "endBound" : BoundingType.SYMMETRIC, "depth" : (getVariable(context, 'eTole')) * mm, "offsetDistance" : 25 * mm});
        }
        {
            var Q0;
            Q0 = qSketchRegion(id + "F5", true);
            extrude(context, id + "F9", {"entities" : qUnion([Q0]), "operationType" : NewBodyOperationType.REMOVE, "endBound" : BoundingType.SYMMETRIC, "oppositeDirection" : true, "depth" : (getVariable(context, 'eTole')) * mm});
        }
        {
            var Q0;
            Q0=makeQuery(id+"F8.opExtrude","SWEPT_BODY",BODY,{"disambiguationData":[OSD([sQuery(id+"F2.wireOp",EDGE,"E45.0"),sQuery(id+"F2.wireOp",EDGE,"E45.1"),sQuery(id+"F2.wireOp",EDGE,"E45.2"),sQuery(id+"F2.wireOp",EDGE,"E45.3"),sQuery(id+"F2.wireOp",EDGE,"E45.4"),sQuery(id+"F2.wireOp",EDGE,"E45.5"),sQuery(id+"F2.wireOp",EDGE,"E53"),sQuery(id+"F2.wireOp",EDGE,"E54"),sQuery(id+"F2.wireOp",EDGE,"E55"),sQuery(id+"F2.wireOp",EDGE,"E56"),sQuery(id+"F2.wireOp",EDGE,"E58"),sQuery(id+"F2.wireOp",EDGE,"E59.MirrorC")])]});
            var Q1;
            Q1=makeQuery(id+"F8.opExtrude","SWEPT_BODY",BODY,{"disambiguationData":[OSD([sQuery(id+"F4.wireOp",EDGE,"E83.1"),sQuery(id+"F4.wireOp",EDGE,"E83.2"),sQuery(id+"F4.wireOp",EDGE,"E83.3"),sQuery(id+"F4.wireOp",EDGE,"E83.4"),sQuery(id+"F4.wireOp",EDGE,"E83.5"),sQuery(id+"F4.wireOp",EDGE,"E83.6"),sQuery(id+"F4.wireOp",EDGE,"E83.7"),sQuery(id+"F4.wireOp",EDGE,"E85"),sQuery(id+"F4.wireOp",EDGE,"E86"),sQuery(id+"F4.wireOp",EDGE,"E93"),sQuery(id+"F4.wireOp",EDGE,"E94"),sQuery(id+"F4.wireOp",EDGE,"E95"),sQuery(id+"F4.wireOp",EDGE,"E96"),sQuery(id+"F4.wireOp",EDGE,"E98.bottom"),sQuery(id+"F4.wireOp",EDGE,"E98.top"),sQuery(id+"F4.wireOp",EDGE,"E98.left"),sQuery(id+"F4.wireOp",EDGE,"E99.trimOffspring"),sQuery(id+"F4.wireOp",EDGE,"E103")])]});
            var Q2;
            Q2=qCreatedBy(makeId("Right.planeOp"),FACE);
            mirror(context, id + "F10", {"entities" : qUnion([Q0, Q1]), "mirrorPlane" : qUnion([Q2])});
        }
        {
            var Q0;
            Q0 = qSketchRegion(id + "F6", true);
            var Q1;
            Q1 = qSketchRegion(id + "F7", true);
            extrude(context, id + "F11", {"entities" : qUnion([Q0, Q1]), "depth" : (getVariable(context, 'eTole')) * mm, "offsetDistance" : 25 * mm});
        }
    });
